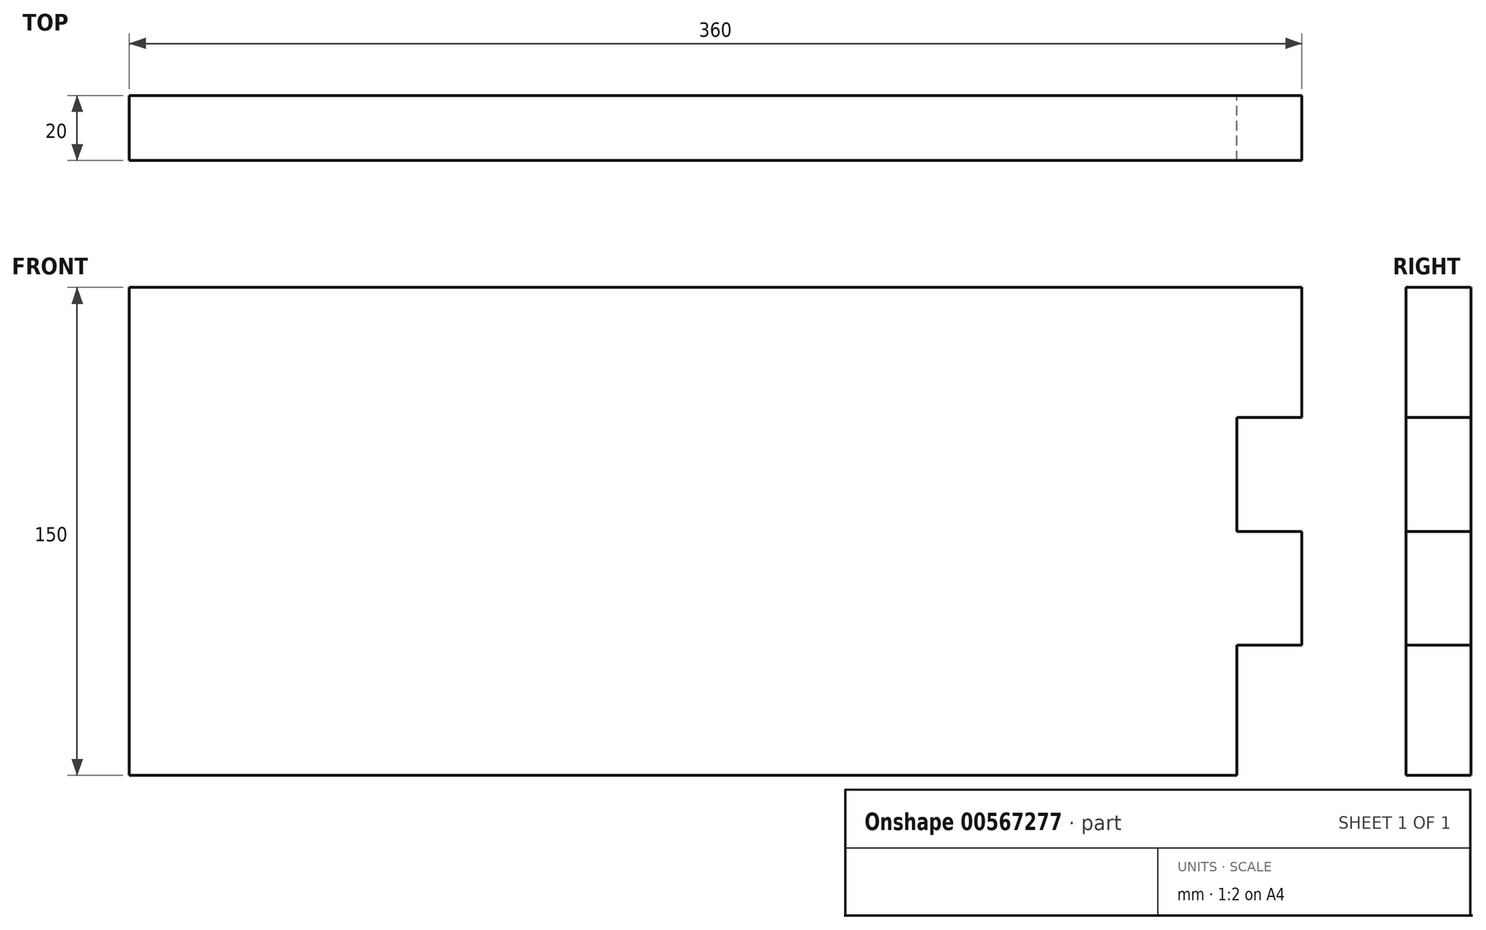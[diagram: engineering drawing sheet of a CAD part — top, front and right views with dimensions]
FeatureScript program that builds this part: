
annotation { "Feature Type Name" : "Feature", "Feature Type Description" : "" }
export const myFeature = defineFeature(function(context is Context, id is Id, definition is map)
    precondition{}
    {
        {
            var Q0;
            Q0=qCreatedBy(makeId("Front.planeOp"),FACE);
            var sketch = newSketch(context, id + "F0", { "sketchPlane" : qUnion([Q0])});
            skLineSegment(sketch, "E0.bottom", {"start": v(-20, 0) * mm, "end": v(-360, 0) * mm});
            skLineSegment(sketch, "E0.top", {"start": v(0, 150) * mm, "end": v(-360, 150) * mm});
            skLineSegment(sketch, "E0.left", {"start": v(0, 40) * mm, "end": v(0, 75) * mm});
            skLineSegment(sketch, "E0.right", {"start": v(-360, 0) * mm, "end": v(-360, 150) * mm});
            skLineSegment(sketch, "E1", {"start": v(-20, 110) * mm, "end": v(-20, 75) * mm});
            skLineSegment(sketch, "E2", {"start": v(0, 75) * mm, "end": v(-20, 75) * mm});
            skLineSegment(sketch, "E3", {"start": v(0, 40) * mm, "end": v(-20, 40) * mm});
            skLineSegment(sketch, "E4", {"start": v(0, 110) * mm, "end": v(-20, 110) * mm});
            skLineSegment(sketch, "E5.trimOffspring", {"start": v(0, 110) * mm, "end": v(0, 150) * mm});
            skPoint(sketch, "E6.orphan", {"position": v(0, 0) * mm});
            skPoint(sketch, "E7.orphan", {"position": v(-20, 150) * mm});
            skLineSegment(sketch, "E8.trimOffspring", {"start": v(-20, 40) * mm, "end": v(-20, 0) * mm});
            skSolve(sketch);
        }
        {
            var Q0;
            Q0=makeQuery(id+"F0.imprint","IMPRINT",FACE,{"disambiguationData":[TD([[makeQuery(id+"F0.imprint","IMPRINT",EDGE,{"derivedFrom":sQuery(id+"F0.wireOp",EDGE,"E0.bottom")}),-1.0]])]});
            extrude(context, id + "F1", {"entities" : qUnion([Q0]), "depth" : 20 * mm, "offsetDistance" : 25.4 * mm});
        }
    });
